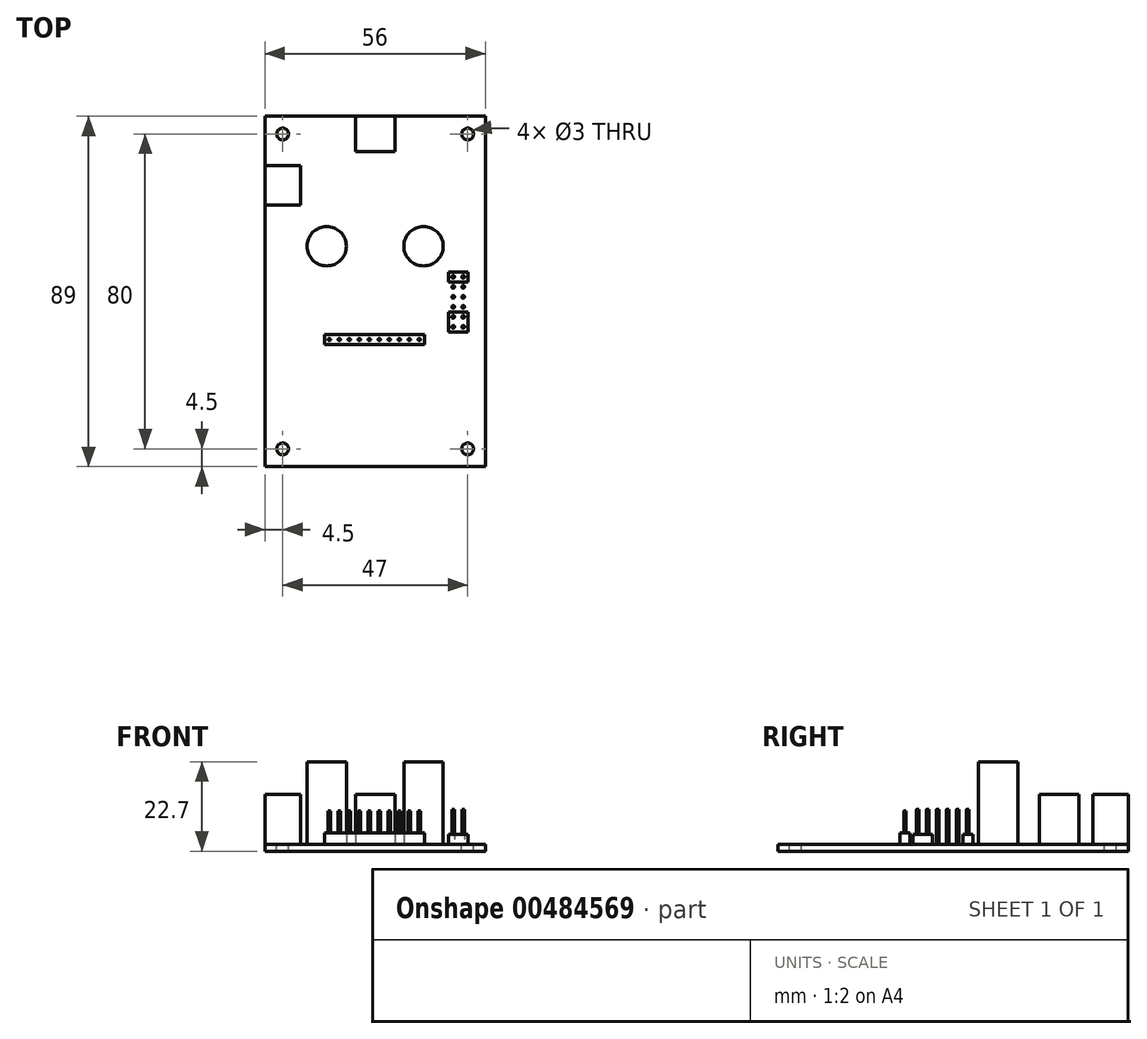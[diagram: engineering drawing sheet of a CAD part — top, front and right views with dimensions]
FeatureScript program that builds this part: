
annotation { "Feature Type Name" : "Feature", "Feature Type Description" : "" }
export const myFeature = defineFeature(function(context is Context, id is Id, definition is map)
    precondition{}
    {
        {
            var Q0;
            Q0=qCreatedBy(makeId("Top.planeOp"),FACE);
            var sketch = newSketch(context, id + "F0", { "sketchPlane" : qUnion([Q0])});
            skLineSegment(sketch, "E0.bottom", {"start": v(28, -44.5) * mm, "end": v(-28, -44.5) * mm});
            skLineSegment(sketch, "E0.top", {"start": v(28, 44.5) * mm, "end": v(-28, 44.5) * mm});
            skLineSegment(sketch, "E0.left", {"start": v(28, -44.5) * mm, "end": v(28, 44.5) * mm});
            skLineSegment(sketch, "E0.right", {"start": v(-28, -44.5) * mm, "end": v(-28, 44.5) * mm});
            skPoint(sketch, "E0.middle", {"position": v(0, 0) * mm});
            skCircle(sketch, "E1", {"center": v(12.3, 11.5) * mm, "radius": 5 * mm});
            skCircle(sketch, "E2", {"center": v(-12.3, 11.5) * mm, "radius": 5 * mm});
            skLineSegment(sketch, "E3", {"start": v(-12.3, 11.5) * mm, "end": v(-12.3, 44.5) * mm, "construction": true});
            skLineSegment(sketch, "E4", {"start": v(-12.3, 11.5) * mm, "end": v(-28, 11.5) * mm, "construction": true});
            skPoint(sketch, "E4.endSnap0", {"position": v(-28, 0) * mm});
            skLineSegment(sketch, "E5", {"start": v(12.3, 11.5) * mm, "end": v(12.3, 44.5) * mm, "construction": true});
            skLineSegment(sketch, "E6", {"start": v(12.3, 11.5) * mm, "end": v(28, 11.5) * mm, "construction": true});
            skCircle(sketch, "E7", {"center": v(-23.5, -40) * mm, "radius": 1.5 * mm});
            skLineSegment(sketch, "E8", {"start": v(-28, -40) * mm, "end": v(-25, -40) * mm, "construction": true});
            skLineSegment(sketch, "E9", {"start": v(-23.5, -44.5) * mm, "end": v(-23.5, -41.5) * mm, "construction": true});
            skCircle(sketch, "E10", {"center": v(23.5, -40) * mm, "radius": 1.5 * mm});
            skLineSegment(sketch, "E11", {"start": v(28, -40) * mm, "end": v(25, -40) * mm, "construction": true});
            skCircle(sketch, "E12", {"center": v(-23.5, 40) * mm, "radius": 1.5 * mm});
            skCircle(sketch, "E13", {"center": v(23.5, 40) * mm, "radius": 1.5 * mm});
            skLineSegment(sketch, "E14", {"start": v(-23.5, 44.5) * mm, "end": v(-23.5, 41.5) * mm, "construction": true});
            skLineSegment(sketch, "E15", {"start": v(0, 44.5) * mm, "end": v(0, -44.5) * mm, "construction": true});
            skLineSegment(sketch, "E16", {"start": v(-5, 35.5) * mm, "end": v(5, 35.5) * mm});
            skPoint(sketch, "E17", {"position": v(0, 35.5) * mm});
            skLineSegment(sketch, "E18", {"start": v(-5, 35.5) * mm, "end": v(-5, 44.5) * mm});
            skLineSegment(sketch, "E19", {"start": v(5, 35.5) * mm, "end": v(5, 44.5) * mm});
            skLineSegment(sketch, "E20", {"start": v(-28, 32) * mm, "end": v(-19, 32) * mm});
            skLineSegment(sketch, "E21", {"start": v(-19, 32) * mm, "end": v(-19, 22) * mm});
            skLineSegment(sketch, "E22", {"start": v(-19, 22) * mm, "end": v(-28, 22) * mm});
            skSolve(sketch);
        }
        {
            var Q0;
            Q0=makeQuery(id+"F0.imprint","IMPRINT",FACE,{"disambiguationData":[TD([[makeQuery(id+"F0.imprint","IMPRINT",EDGE,{"derivedFrom":sQuery(id+"F0.wireOp",EDGE,"E1")}),1.0]])]});
            var Q1;
            Q1=makeQuery(id+"F0.imprint","IMPRINT",FACE,{"disambiguationData":[TD([[makeQuery(id+"F0.imprint","IMPRINT",EDGE,{"derivedFrom":sQuery(id+"F0.wireOp",EDGE,"E2")}),1.0]])]});
            extrude(context, id + "F1", {"entities" : qUnion([Q0, Q1]), "depth" : 21 * mm});
        }
        {
            var Q0;
            Q0=makeQuery(id+"F0.imprint","IMPRINT",FACE,{"disambiguationData":[TD([[makeQuery(id+"F0.imprint","IMPRINT",EDGE,{"derivedFrom":sQuery(id+"F0.wireOp",EDGE,"E1")}),1.0]])]});
            var Q1;
            Q1=makeQuery(id+"F0.imprint","IMPRINT",FACE,{"disambiguationData":[TD([[makeQuery(id+"F0.imprint","IMPRINT",EDGE,{"derivedFrom":sQuery(id+"F0.wireOp",EDGE,"E2")}),1.0]])]});
            var Q2;
            Q2=makeQuery(id+"F0.imprint","IMPRINT",FACE,{"disambiguationData":[TD([[makeQuery(id+"F0.imprint","IMPRINT",EDGE,{"derivedFrom":sQuery(id+"F0.wireOp",EDGE,"E0.bottom")}),-1.0]])]});
            var Q3;
            {var subQ0=sQuery(id+"F0.wireOp",EDGE,"QGclrdqu-3yr5-Tu7r-SbyD-ftDcwHvLKRqM");Q3=makeQuery(id+"F0.imprint","IMPRINT",FACE,{"disambiguationData":[TD([[makeQuery(id+"F0.imprint","IMPRINT",EDGE,{"derivedFrom":subQ0}),1.0]])]});}
            var Q4;
            {var subQ0=sQuery(id+"F0.wireOp",EDGE,"E20");Q4=makeQuery(id+"F0.imprint","IMPRINT",FACE,{"disambiguationData":[TD([[makeQuery(id+"F0.imprint","IMPRINT",EDGE,{"derivedFrom":subQ0}),-1.0]])]});}
            var Q5;
            Q5=makeQuery(id+"F0.imprint","IMPRINT",FACE,{"disambiguationData":[TD([[makeQuery(id+"F0.imprint","IMPRINT",EDGE,{"derivedFrom":sQuery(id+"F0.wireOp",EDGE,"E16")}),1.0]])]});
            extrude(context, id + "F2", {"entities" : qUnion([Q0, Q1, Q2, Q3, Q4, Q5]), "depth" : -1.7 * mm});
        }
        {
            var Q0;
            Q0=makeQuery(id+"F0.imprint","IMPRINT",FACE,{"disambiguationData":[TD([[makeQuery(id+"F0.imprint","IMPRINT",EDGE,{"derivedFrom":sQuery(id+"F0.wireOp",EDGE,"E16")}),1.0]])]});
            var Q1;
            {var subQ0=sQuery(id+"F0.wireOp",EDGE,"E20");Q1=makeQuery(id+"F0.imprint","IMPRINT",FACE,{"disambiguationData":[TD([[makeQuery(id+"F0.imprint","IMPRINT",EDGE,{"derivedFrom":subQ0}),-1.0]])]});}
            extrude(context, id + "F3", {"entities" : qUnion([Q0, Q1]), "operationType" : NewBodyOperationType.ADD, "depth" : 12.7 * mm});
        }
        {
            var Q0;
            Q0=makeQuery(id+"F2.opExtrude","CAP_FACE",FACE,{"disambiguationData":[OSD([sQuery(id+"F0.wireOp",EDGE,"E0.bottom"),sQuery(id+"F0.wireOp",EDGE,"E0.top"),sQuery(id+"F0.wireOp",EDGE,"E0.left"),sQuery(id+"F0.wireOp",EDGE,"E0.right"),sQuery(id+"F0.wireOp",EDGE,"E7"),sQuery(id+"F0.wireOp",EDGE,"E10"),sQuery(id+"F0.wireOp",EDGE,"E12"),sQuery(id+"F0.wireOp",EDGE,"E13")])],"isStart":true});
            var sketch = newSketch(context, id + "F4", { "sketchPlane" : qUnion([Q0])});
            skLineSegment(sketch, "E23.bottom", {"start": v(18.6, -7.7) * mm, "end": v(23.6, -7.7) * mm});
            skLineSegment(sketch, "E23.top", {"start": v(18.6, -10.25) * mm, "end": v(23.6, -10.25) * mm});
            skLineSegment(sketch, "E23.left", {"start": v(18.6, -7.7) * mm, "end": v(18.6, -10.25) * mm});
            skLineSegment(sketch, "E23.right", {"start": v(23.6, -7.7) * mm, "end": v(23.6, -10.25) * mm});
            skLineSegment(sketch, "E24", {"start": v(18.6, -8.98) * mm, "end": v(23.6, -8.98) * mm, "construction": true});
            skPoint(sketch, "E25", {"position": v(21.1, -8.98) * mm});
            skCircle(sketch, "E26", {"center": v(19.83, -8.98) * mm, "radius": 0.35 * mm});
            skCircle(sketch, "E27", {"center": v(22.37, -8.98) * mm, "radius": 0.35 * mm});
            skLineSegment(sketch, "E28.0.1.0", {"start": v(18.6, -5.17) * mm, "end": v(23.6, -5.17) * mm});
            skLineSegment(sketch, "E28.0.1.2", {"start": v(18.6, -5.17) * mm, "end": v(18.6, -7.7) * mm});
            skLineSegment(sketch, "E28.0.1.3", {"start": v(23.6, -5.17) * mm, "end": v(23.6, -7.7) * mm});
            skLineSegment(sketch, "E28.0.1.4", {"start": v(18.6, -6.44) * mm, "end": v(23.6, -6.44) * mm, "construction": true});
            skPoint(sketch, "E28.0.1.5", {"position": v(21.1, -6.44) * mm});
            skCircle(sketch, "E28.0.1.6", {"center": v(19.83, -6.44) * mm, "radius": 0.35 * mm});
            skCircle(sketch, "E28.0.1.7", {"center": v(22.37, -6.44) * mm, "radius": 0.35 * mm});
            skLineSegment(sketch, "E28.0.2.0", {"start": v(18.6, -2.63) * mm, "end": v(23.6, -2.63) * mm});
            skLineSegment(sketch, "E28.0.2.1", {"start": v(18.6, -5.17) * mm, "end": v(23.6, -5.17) * mm});
            skLineSegment(sketch, "E28.0.2.2", {"start": v(18.6, -2.63) * mm, "end": v(18.6, -5.17) * mm});
            skLineSegment(sketch, "E28.0.2.3", {"start": v(23.6, -2.63) * mm, "end": v(23.6, -5.17) * mm});
            skLineSegment(sketch, "E28.0.2.4", {"start": v(18.6, -3.9) * mm, "end": v(23.6, -3.9) * mm, "construction": true});
            skPoint(sketch, "E28.0.2.5", {"position": v(21.1, -3.9) * mm});
            skCircle(sketch, "E28.0.2.6", {"center": v(19.83, -3.9) * mm, "radius": 0.35 * mm});
            skCircle(sketch, "E28.0.2.7", {"center": v(22.37, -3.9) * mm, "radius": 0.35 * mm});
            skLineSegment(sketch, "E28.0.3.0", {"start": v(18.6, -0.09) * mm, "end": v(23.6, -0.09) * mm});
            skLineSegment(sketch, "E28.0.3.1", {"start": v(18.6, -2.63) * mm, "end": v(23.6, -2.63) * mm});
            skLineSegment(sketch, "E28.0.3.2", {"start": v(18.6, -0.09) * mm, "end": v(18.6, -2.63) * mm});
            skLineSegment(sketch, "E28.0.3.3", {"start": v(23.6, -0.09) * mm, "end": v(23.6, -2.63) * mm});
            skLineSegment(sketch, "E28.0.3.4", {"start": v(18.6, -1.36) * mm, "end": v(23.6, -1.36) * mm, "construction": true});
            skPoint(sketch, "E28.0.3.5", {"position": v(21.1, -1.36) * mm});
            skCircle(sketch, "E28.0.3.6", {"center": v(19.83, -1.36) * mm, "radius": 0.35 * mm});
            skCircle(sketch, "E28.0.3.7", {"center": v(22.37, -1.36) * mm, "radius": 0.35 * mm});
            skLineSegment(sketch, "E28.0.4.0", {"start": v(18.6, 2.45) * mm, "end": v(23.6, 2.45) * mm});
            skLineSegment(sketch, "E28.0.4.1", {"start": v(18.6, -0.09) * mm, "end": v(23.6, -0.09) * mm});
            skLineSegment(sketch, "E28.0.4.2", {"start": v(18.6, 2.45) * mm, "end": v(18.6, -0.09) * mm});
            skLineSegment(sketch, "E28.0.4.3", {"start": v(23.6, 2.45) * mm, "end": v(23.6, -0.09) * mm});
            skLineSegment(sketch, "E28.0.4.4", {"start": v(18.6, 1.18) * mm, "end": v(23.6, 1.18) * mm, "construction": true});
            skPoint(sketch, "E28.0.4.5", {"position": v(21.1, 1.18) * mm});
            skCircle(sketch, "E28.0.4.6", {"center": v(19.83, 1.18) * mm, "radius": 0.35 * mm});
            skCircle(sketch, "E28.0.4.7", {"center": v(22.37, 1.18) * mm, "radius": 0.35 * mm});
            skLineSegment(sketch, "E28.0.5.0", {"start": v(18.6, 5) * mm, "end": v(23.6, 5) * mm});
            skLineSegment(sketch, "E28.0.5.1", {"start": v(18.6, 2.45) * mm, "end": v(23.6, 2.45) * mm});
            skLineSegment(sketch, "E28.0.5.2", {"start": v(18.6, 5) * mm, "end": v(18.6, 2.45) * mm});
            skLineSegment(sketch, "E28.0.5.3", {"start": v(23.6, 5) * mm, "end": v(23.6, 2.45) * mm});
            skLineSegment(sketch, "E28.0.5.4", {"start": v(18.6, 3.72) * mm, "end": v(23.6, 3.72) * mm, "construction": true});
            skPoint(sketch, "E28.0.5.5", {"position": v(21.1, 3.72) * mm});
            skCircle(sketch, "E28.0.5.6", {"center": v(19.83, 3.72) * mm, "radius": 0.35 * mm});
            skCircle(sketch, "E28.0.5.7", {"center": v(22.37, 3.72) * mm, "radius": 0.35 * mm});
            skLineSegment(sketch, "E28.direction1", {"start": v(18.6, -10.25) * mm, "end": v(43.6, -10.25) * mm, "construction": true});
            skLineSegment(sketch, "E28.direction2", {"start": v(18.6, -10.25) * mm, "end": v(18.6, -7.7) * mm, "construction": true});
            skLineSegment(sketch, "E29.bottom", {"start": v(9.96, -10.96) * mm, "end": v(12.5, -10.96) * mm});
            skLineSegment(sketch, "E29.top", {"start": v(9.96, -13.5) * mm, "end": v(12.5, -13.5) * mm});
            skLineSegment(sketch, "E29.left", {"start": v(9.96, -10.96) * mm, "end": v(9.96, -13.5) * mm});
            skLineSegment(sketch, "E29.right", {"start": v(12.5, -10.96) * mm, "end": v(12.5, -13.5) * mm});
            skLineSegment(sketch, "E30", {"start": v(9.96, -12.23) * mm, "end": v(12.5, -12.23) * mm, "construction": true});
            skPoint(sketch, "E31", {"position": v(11.23, -12.23) * mm});
            skCircle(sketch, "E32", {"center": v(11.23, -12.23) * mm, "radius": 0.3 * mm});
            skLineSegment(sketch, "E33.1.0.0", {"start": v(7.42, -13.5) * mm, "end": v(9.96, -13.5) * mm});
            skLineSegment(sketch, "E33.1.0.1", {"start": v(7.42, -10.96) * mm, "end": v(7.42, -13.5) * mm});
            skLineSegment(sketch, "E33.1.0.3", {"start": v(7.42, -12.23) * mm, "end": v(9.96, -12.23) * mm, "construction": true});
            skPoint(sketch, "E33.1.0.4", {"position": v(8.7, -12.23) * mm});
            skCircle(sketch, "E33.1.0.5", {"center": v(8.7, -12.23) * mm, "radius": 0.3 * mm});
            skLineSegment(sketch, "E33.1.0.6", {"start": v(7.42, -10.96) * mm, "end": v(9.96, -10.96) * mm});
            skLineSegment(sketch, "E33.2.0.0", {"start": v(4.88, -13.5) * mm, "end": v(7.42, -13.5) * mm});
            skLineSegment(sketch, "E33.2.0.1", {"start": v(4.88, -10.96) * mm, "end": v(4.88, -13.5) * mm});
            skLineSegment(sketch, "E33.2.0.2", {"start": v(7.42, -10.96) * mm, "end": v(7.42, -13.5) * mm});
            skLineSegment(sketch, "E33.2.0.3", {"start": v(4.88, -12.23) * mm, "end": v(7.42, -12.23) * mm, "construction": true});
            skPoint(sketch, "E33.2.0.4", {"position": v(6.15, -12.23) * mm});
            skCircle(sketch, "E33.2.0.5", {"center": v(6.15, -12.23) * mm, "radius": 0.3 * mm});
            skLineSegment(sketch, "E33.2.0.6", {"start": v(4.88, -10.96) * mm, "end": v(7.42, -10.96) * mm});
            skLineSegment(sketch, "E33.3.0.0", {"start": v(2.34, -13.5) * mm, "end": v(4.88, -13.5) * mm});
            skLineSegment(sketch, "E33.3.0.1", {"start": v(2.34, -10.96) * mm, "end": v(2.34, -13.5) * mm});
            skLineSegment(sketch, "E33.3.0.2", {"start": v(4.88, -10.96) * mm, "end": v(4.88, -13.5) * mm});
            skLineSegment(sketch, "E33.3.0.3", {"start": v(2.34, -12.23) * mm, "end": v(4.88, -12.23) * mm, "construction": true});
            skPoint(sketch, "E33.3.0.4", {"position": v(3.61, -12.23) * mm});
            skCircle(sketch, "E33.3.0.5", {"center": v(3.61, -12.23) * mm, "radius": 0.3 * mm});
            skLineSegment(sketch, "E33.3.0.6", {"start": v(2.34, -10.96) * mm, "end": v(4.88, -10.96) * mm});
            skLineSegment(sketch, "E33.4.0.0", {"start": v(-0.2, -13.5) * mm, "end": v(2.34, -13.5) * mm});
            skLineSegment(sketch, "E33.4.0.1", {"start": v(-0.2, -10.96) * mm, "end": v(-0.2, -13.5) * mm});
            skLineSegment(sketch, "E33.4.0.2", {"start": v(2.34, -10.96) * mm, "end": v(2.34, -13.5) * mm});
            skLineSegment(sketch, "E33.4.0.3", {"start": v(-0.2, -12.23) * mm, "end": v(2.34, -12.23) * mm, "construction": true});
            skPoint(sketch, "E33.4.0.4", {"position": v(1.07, -12.23) * mm});
            skCircle(sketch, "E33.4.0.5", {"center": v(1.07, -12.23) * mm, "radius": 0.3 * mm});
            skLineSegment(sketch, "E33.4.0.6", {"start": v(-0.2, -10.96) * mm, "end": v(2.34, -10.96) * mm});
            skLineSegment(sketch, "E33.5.0.0", {"start": v(-2.74, -13.5) * mm, "end": v(-0.2, -13.5) * mm});
            skLineSegment(sketch, "E33.5.0.1", {"start": v(-2.74, -10.96) * mm, "end": v(-2.74, -13.5) * mm});
            skLineSegment(sketch, "E33.5.0.2", {"start": v(-0.2, -10.96) * mm, "end": v(-0.2, -13.5) * mm});
            skLineSegment(sketch, "E33.5.0.3", {"start": v(-2.74, -12.23) * mm, "end": v(-0.2, -12.23) * mm, "construction": true});
            skPoint(sketch, "E33.5.0.4", {"position": v(-1.47, -12.23) * mm});
            skCircle(sketch, "E33.5.0.5", {"center": v(-1.47, -12.23) * mm, "radius": 0.3 * mm});
            skLineSegment(sketch, "E33.5.0.6", {"start": v(-2.74, -10.96) * mm, "end": v(-0.2, -10.96) * mm});
            skLineSegment(sketch, "E33.6.0.0", {"start": v(-5.28, -13.5) * mm, "end": v(-2.74, -13.5) * mm});
            skLineSegment(sketch, "E33.6.0.1", {"start": v(-5.28, -10.96) * mm, "end": v(-5.28, -13.5) * mm});
            skLineSegment(sketch, "E33.6.0.2", {"start": v(-2.74, -10.96) * mm, "end": v(-2.74, -13.5) * mm});
            skLineSegment(sketch, "E33.6.0.3", {"start": v(-5.28, -12.23) * mm, "end": v(-2.74, -12.23) * mm, "construction": true});
            skPoint(sketch, "E33.6.0.4", {"position": v(-4, -12.23) * mm});
            skCircle(sketch, "E33.6.0.5", {"center": v(-4, -12.23) * mm, "radius": 0.3 * mm});
            skLineSegment(sketch, "E33.6.0.6", {"start": v(-5.28, -10.96) * mm, "end": v(-2.74, -10.96) * mm});
            skLineSegment(sketch, "E33.7.0.0", {"start": v(-7.82, -13.5) * mm, "end": v(-5.28, -13.5) * mm});
            skLineSegment(sketch, "E33.7.0.1", {"start": v(-7.82, -10.96) * mm, "end": v(-7.82, -13.5) * mm});
            skLineSegment(sketch, "E33.7.0.2", {"start": v(-5.28, -10.96) * mm, "end": v(-5.28, -13.5) * mm});
            skLineSegment(sketch, "E33.7.0.3", {"start": v(-7.82, -12.23) * mm, "end": v(-5.28, -12.23) * mm, "construction": true});
            skPoint(sketch, "E33.7.0.4", {"position": v(-6.55, -12.23) * mm});
            skCircle(sketch, "E33.7.0.5", {"center": v(-6.55, -12.23) * mm, "radius": 0.3 * mm});
            skLineSegment(sketch, "E33.7.0.6", {"start": v(-7.82, -10.96) * mm, "end": v(-5.28, -10.96) * mm});
            skLineSegment(sketch, "E33.8.0.0", {"start": v(-10.36, -13.5) * mm, "end": v(-7.82, -13.5) * mm});
            skLineSegment(sketch, "E33.8.0.1", {"start": v(-10.36, -10.96) * mm, "end": v(-10.36, -13.5) * mm});
            skLineSegment(sketch, "E33.8.0.2", {"start": v(-7.82, -10.96) * mm, "end": v(-7.82, -13.5) * mm});
            skLineSegment(sketch, "E33.8.0.3", {"start": v(-10.36, -12.23) * mm, "end": v(-7.82, -12.23) * mm, "construction": true});
            skPoint(sketch, "E33.8.0.4", {"position": v(-9.1, -12.23) * mm});
            skCircle(sketch, "E33.8.0.5", {"center": v(-9.1, -12.23) * mm, "radius": 0.3 * mm});
            skLineSegment(sketch, "E33.8.0.6", {"start": v(-10.36, -10.96) * mm, "end": v(-7.82, -10.96) * mm});
            skLineSegment(sketch, "E33.9.0.0", {"start": v(-12.9, -13.5) * mm, "end": v(-10.36, -13.5) * mm});
            skLineSegment(sketch, "E33.9.0.1", {"start": v(-12.9, -10.96) * mm, "end": v(-12.9, -13.5) * mm});
            skLineSegment(sketch, "E33.9.0.2", {"start": v(-10.36, -10.96) * mm, "end": v(-10.36, -13.5) * mm});
            skLineSegment(sketch, "E33.9.0.3", {"start": v(-12.9, -12.23) * mm, "end": v(-10.36, -12.23) * mm, "construction": true});
            skPoint(sketch, "E33.9.0.4", {"position": v(-11.63, -12.23) * mm});
            skCircle(sketch, "E33.9.0.5", {"center": v(-11.63, -12.23) * mm, "radius": 0.3 * mm});
            skLineSegment(sketch, "E33.9.0.6", {"start": v(-12.9, -10.96) * mm, "end": v(-10.36, -10.96) * mm});
            skLineSegment(sketch, "E33.direction1", {"start": v(9.96, -13.5) * mm, "end": v(7.42, -13.5) * mm, "construction": true});
            skSolve(sketch);
        }
        {
            var Q0;
            Q0=makeQuery(id+"F4.imprint","IMPRINT",FACE,{"disambiguationData":[TD([[makeQuery(id+"F4.imprint","IMPRINT",EDGE,{"derivedFrom":sQuery(id+"F4.wireOp",EDGE,"E28.0.1.6")}),1.0]])]});
            var Q1;
            Q1=makeQuery(id+"F4.imprint","IMPRINT",FACE,{"disambiguationData":[TD([[makeQuery(id+"F4.imprint","IMPRINT",EDGE,{"derivedFrom":sQuery(id+"F4.wireOp",EDGE,"E28.0.1.7")}),1.0]])]});
            var Q2;
            Q2=makeQuery(id+"F4.imprint","IMPRINT",FACE,{"disambiguationData":[TD([[makeQuery(id+"F4.imprint","IMPRINT",EDGE,{"derivedFrom":sQuery(id+"F4.wireOp",EDGE,"E27")}),1.0]])]});
            var Q3;
            Q3=makeQuery(id+"F4.imprint","IMPRINT",FACE,{"disambiguationData":[TD([[makeQuery(id+"F4.imprint","IMPRINT",EDGE,{"derivedFrom":sQuery(id+"F4.wireOp",EDGE,"E26")}),1.0]])]});
            var Q4;
            Q4=makeQuery(id+"F4.imprint","IMPRINT",FACE,{"disambiguationData":[TD([[makeQuery(id+"F4.imprint","IMPRINT",EDGE,{"derivedFrom":sQuery(id+"F4.wireOp",EDGE,"E28.0.2.6")}),1.0]])]});
            var Q5;
            Q5=makeQuery(id+"F4.imprint","IMPRINT",FACE,{"disambiguationData":[TD([[makeQuery(id+"F4.imprint","IMPRINT",EDGE,{"derivedFrom":sQuery(id+"F4.wireOp",EDGE,"E28.0.2.7")}),1.0]])]});
            var Q6;
            Q6=makeQuery(id+"F4.imprint","IMPRINT",FACE,{"disambiguationData":[TD([[makeQuery(id+"F4.imprint","IMPRINT",EDGE,{"derivedFrom":sQuery(id+"F4.wireOp",EDGE,"E28.0.4.6")}),1.0]])]});
            var Q7;
            Q7=makeQuery(id+"F4.imprint","IMPRINT",FACE,{"disambiguationData":[TD([[makeQuery(id+"F4.imprint","IMPRINT",EDGE,{"derivedFrom":sQuery(id+"F4.wireOp",EDGE,"E28.0.3.6")}),1.0]])]});
            var Q8;
            Q8=makeQuery(id+"F4.imprint","IMPRINT",FACE,{"disambiguationData":[TD([[makeQuery(id+"F4.imprint","IMPRINT",EDGE,{"derivedFrom":sQuery(id+"F4.wireOp",EDGE,"E28.0.3.7")}),1.0]])]});
            var Q9;
            Q9=makeQuery(id+"F4.imprint","IMPRINT",FACE,{"disambiguationData":[TD([[makeQuery(id+"F4.imprint","IMPRINT",EDGE,{"derivedFrom":sQuery(id+"F4.wireOp",EDGE,"E28.0.4.7")}),1.0]])]});
            var Q10;
            Q10=makeQuery(id+"F4.imprint","IMPRINT",FACE,{"disambiguationData":[TD([[makeQuery(id+"F4.imprint","IMPRINT",EDGE,{"derivedFrom":sQuery(id+"F4.wireOp",EDGE,"E28.0.5.7")}),1.0]])]});
            var Q11;
            Q11=makeQuery(id+"F4.imprint","IMPRINT",FACE,{"disambiguationData":[TD([[makeQuery(id+"F4.imprint","IMPRINT",EDGE,{"derivedFrom":sQuery(id+"F4.wireOp",EDGE,"E28.0.5.6")}),1.0]])]});
            extrude(context, id + "F5", {"entities" : qUnion([Q0, Q1, Q2, Q3, Q4, Q5, Q6, Q7, Q8, Q9, Q10, Q11]), "operationType" : NewBodyOperationType.ADD, "depth" : 8.9 * mm});
        }
        {
            var Q0;
            Q0=makeQuery(id+"F4.imprint","IMPRINT",FACE,{"disambiguationData":[TD([[makeQuery(id+"F4.imprint","IMPRINT",EDGE,{"derivedFrom":sQuery(id+"F4.wireOp",EDGE,"E28.0.3.1")}),1.0]])]});
            var Q1;
            Q1=makeQuery(id+"F4.imprint","IMPRINT",FACE,{"disambiguationData":[TD([[makeQuery(id+"F4.imprint","IMPRINT",EDGE,{"derivedFrom":sQuery(id+"F4.wireOp",EDGE,"E28.0.2.1")}),1.0]])]});
            var Q2;
            Q2=makeQuery(id+"F4.imprint","IMPRINT",FACE,{"disambiguationData":[TD([[makeQuery(id+"F4.imprint","IMPRINT",EDGE,{"derivedFrom":sQuery(id+"F4.wireOp",EDGE,"E23.bottom")}),1.0]])]});
            var Q3;
            Q3=makeQuery(id+"F4.imprint","IMPRINT",FACE,{"disambiguationData":[TD([[makeQuery(id+"F4.imprint","IMPRINT",EDGE,{"derivedFrom":sQuery(id+"F4.wireOp",EDGE,"E28.0.4.1")}),1.0]])]});
            var Q4;
            Q4=makeQuery(id+"F4.imprint","IMPRINT",FACE,{"disambiguationData":[TD([[makeQuery(id+"F4.imprint","IMPRINT",EDGE,{"derivedFrom":sQuery(id+"F4.wireOp",EDGE,"E28.0.5.0")}),-1.0]])]});
            var Q5;
            Q5=makeQuery(id+"F4.imprint","IMPRINT",FACE,{"disambiguationData":[TD([[makeQuery(id+"F4.imprint","IMPRINT",EDGE,{"derivedFrom":sQuery(id+"F4.wireOp",EDGE,"E23.top")}),1.0]])]});
            extrude(context, id + "F6", {"entities" : qUnion([Q0, Q1, Q2, Q3, Q4, Q5]), "operationType" : NewBodyOperationType.ADD, "depth" : 2.54 * mm});
        }
        {
            var Q0;
            Q0=makeQuery(id+"F4.imprint","IMPRINT",FACE,{"disambiguationData":[TD([[makeQuery(id+"F4.imprint","IMPRINT",EDGE,{"derivedFrom":sQuery(id+"F4.wireOp",EDGE,"E33.9.0.5")}),1.0]])]});
            var Q1;
            Q1=makeQuery(id+"F4.imprint","IMPRINT",FACE,{"disambiguationData":[TD([[makeQuery(id+"F4.imprint","IMPRINT",EDGE,{"derivedFrom":sQuery(id+"F4.wireOp",EDGE,"E33.8.0.5")}),1.0]])]});
            var Q2;
            Q2=makeQuery(id+"F4.imprint","IMPRINT",FACE,{"disambiguationData":[TD([[makeQuery(id+"F4.imprint","IMPRINT",EDGE,{"derivedFrom":sQuery(id+"F4.wireOp",EDGE,"E33.7.0.5")}),1.0]])]});
            var Q3;
            Q3=makeQuery(id+"F4.imprint","IMPRINT",FACE,{"disambiguationData":[TD([[makeQuery(id+"F4.imprint","IMPRINT",EDGE,{"derivedFrom":sQuery(id+"F4.wireOp",EDGE,"E33.6.0.5")}),1.0]])]});
            var Q4;
            Q4=makeQuery(id+"F4.imprint","IMPRINT",FACE,{"disambiguationData":[TD([[makeQuery(id+"F4.imprint","IMPRINT",EDGE,{"derivedFrom":sQuery(id+"F4.wireOp",EDGE,"E33.5.0.5")}),1.0]])]});
            var Q5;
            Q5=makeQuery(id+"F4.imprint","IMPRINT",FACE,{"disambiguationData":[TD([[makeQuery(id+"F4.imprint","IMPRINT",EDGE,{"derivedFrom":sQuery(id+"F4.wireOp",EDGE,"E33.4.0.5")}),1.0]])]});
            var Q6;
            Q6=makeQuery(id+"F4.imprint","IMPRINT",FACE,{"disambiguationData":[TD([[makeQuery(id+"F4.imprint","IMPRINT",EDGE,{"derivedFrom":sQuery(id+"F4.wireOp",EDGE,"E33.3.0.5")}),1.0]])]});
            var Q7;
            Q7=makeQuery(id+"F4.imprint","IMPRINT",FACE,{"disambiguationData":[TD([[makeQuery(id+"F4.imprint","IMPRINT",EDGE,{"derivedFrom":sQuery(id+"F4.wireOp",EDGE,"E33.2.0.5")}),1.0]])]});
            var Q8;
            Q8=makeQuery(id+"F4.imprint","IMPRINT",FACE,{"disambiguationData":[TD([[makeQuery(id+"F4.imprint","IMPRINT",EDGE,{"derivedFrom":sQuery(id+"F4.wireOp",EDGE,"E33.1.0.5")}),1.0]])]});
            var Q9;
            Q9=makeQuery(id+"F4.imprint","IMPRINT",FACE,{"disambiguationData":[TD([[makeQuery(id+"F4.imprint","IMPRINT",EDGE,{"derivedFrom":sQuery(id+"F4.wireOp",EDGE,"E32")}),1.0]])]});
            extrude(context, id + "F7", {"entities" : qUnion([Q0, Q1, Q2, Q3, Q4, Q5, Q6, Q7, Q8, Q9]), "operationType" : NewBodyOperationType.ADD, "depth" : 8.5 * mm});
        }
        {
            var Q0;
            Q0=makeQuery(id+"F4.imprint","IMPRINT",FACE,{"disambiguationData":[TD([[makeQuery(id+"F4.imprint","IMPRINT",EDGE,{"derivedFrom":sQuery(id+"F4.wireOp",EDGE,"E33.9.0.0")}),1.0]])]});
            var Q1;
            Q1=makeQuery(id+"F4.imprint","IMPRINT",FACE,{"disambiguationData":[TD([[makeQuery(id+"F4.imprint","IMPRINT",EDGE,{"derivedFrom":sQuery(id+"F4.wireOp",EDGE,"E33.8.0.0")}),1.0]])]});
            var Q2;
            Q2=makeQuery(id+"F4.imprint","IMPRINT",FACE,{"disambiguationData":[TD([[makeQuery(id+"F4.imprint","IMPRINT",EDGE,{"derivedFrom":sQuery(id+"F4.wireOp",EDGE,"E33.7.0.0")}),1.0]])]});
            var Q3;
            Q3=makeQuery(id+"F4.imprint","IMPRINT",FACE,{"disambiguationData":[TD([[makeQuery(id+"F4.imprint","IMPRINT",EDGE,{"derivedFrom":sQuery(id+"F4.wireOp",EDGE,"E33.6.0.0")}),1.0]])]});
            var Q4;
            Q4=makeQuery(id+"F4.imprint","IMPRINT",FACE,{"disambiguationData":[TD([[makeQuery(id+"F4.imprint","IMPRINT",EDGE,{"derivedFrom":sQuery(id+"F4.wireOp",EDGE,"E33.5.0.0")}),1.0]])]});
            var Q5;
            Q5=makeQuery(id+"F4.imprint","IMPRINT",FACE,{"disambiguationData":[TD([[makeQuery(id+"F4.imprint","IMPRINT",EDGE,{"derivedFrom":sQuery(id+"F4.wireOp",EDGE,"E33.4.0.0")}),1.0]])]});
            var Q6;
            Q6=makeQuery(id+"F4.imprint","IMPRINT",FACE,{"disambiguationData":[TD([[makeQuery(id+"F4.imprint","IMPRINT",EDGE,{"derivedFrom":sQuery(id+"F4.wireOp",EDGE,"E33.3.0.0")}),1.0]])]});
            var Q7;
            Q7=makeQuery(id+"F4.imprint","IMPRINT",FACE,{"disambiguationData":[TD([[makeQuery(id+"F4.imprint","IMPRINT",EDGE,{"derivedFrom":sQuery(id+"F4.wireOp",EDGE,"E33.2.0.0")}),1.0]])]});
            var Q8;
            Q8=makeQuery(id+"F4.imprint","IMPRINT",FACE,{"disambiguationData":[TD([[makeQuery(id+"F4.imprint","IMPRINT",EDGE,{"derivedFrom":sQuery(id+"F4.wireOp",EDGE,"E33.1.0.0")}),1.0]])]});
            var Q9;
            Q9=makeQuery(id+"F4.imprint","IMPRINT",FACE,{"disambiguationData":[TD([[makeQuery(id+"F4.imprint","IMPRINT",EDGE,{"derivedFrom":sQuery(id+"F4.wireOp",EDGE,"E29.bottom")}),-1.0]])]});
            extrude(context, id + "F8", {"entities" : qUnion([Q0, Q1, Q2, Q3, Q4, Q5, Q6, Q7, Q8, Q9]), "operationType" : NewBodyOperationType.ADD, "depth" : 3 * mm});
        }
    });
